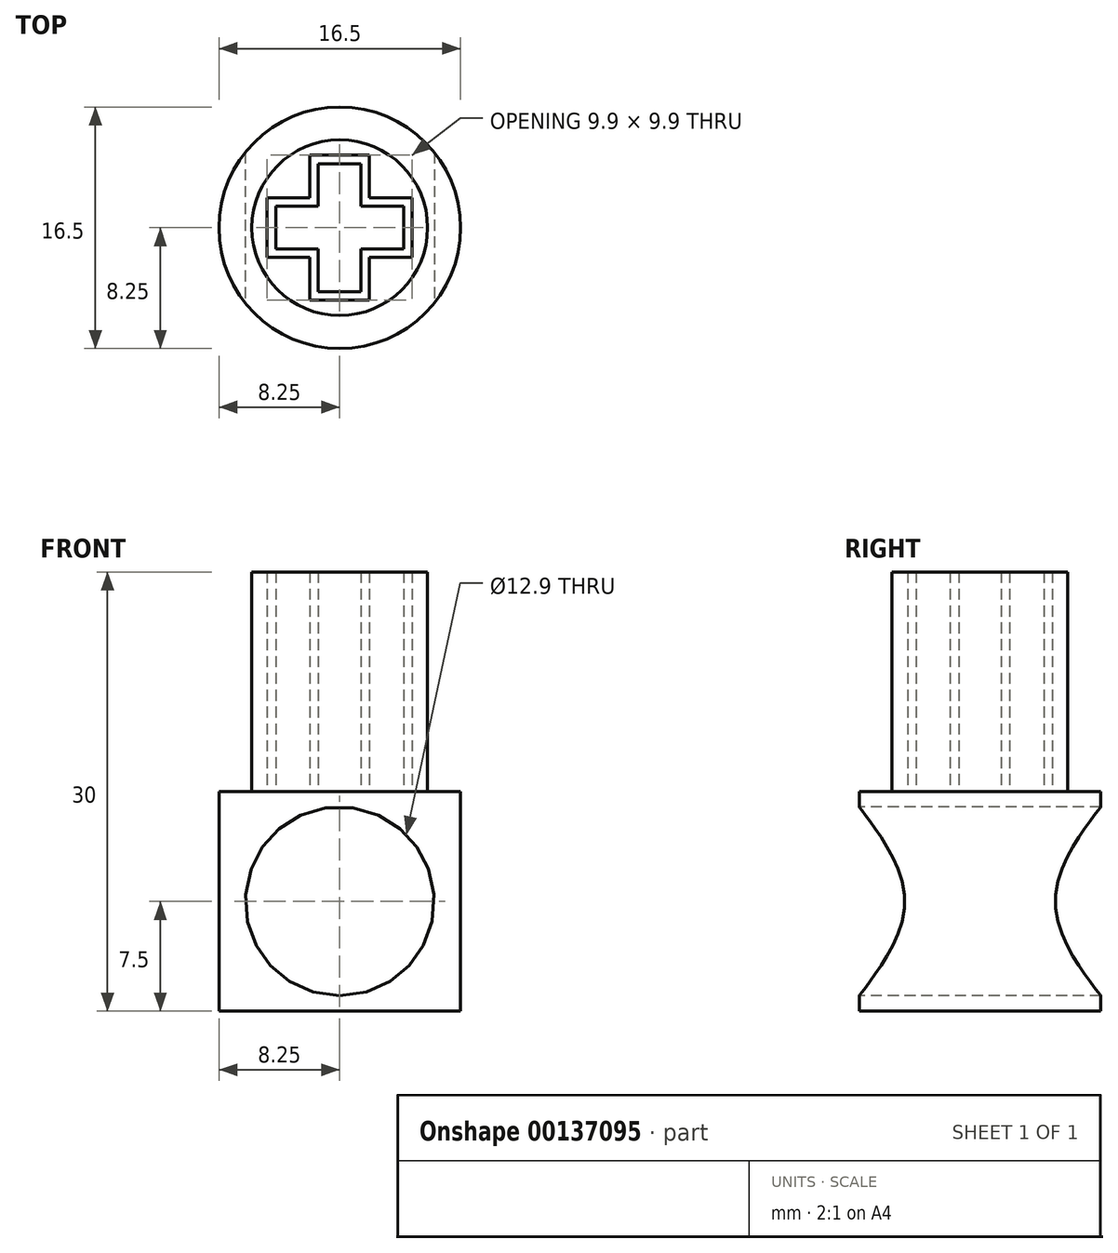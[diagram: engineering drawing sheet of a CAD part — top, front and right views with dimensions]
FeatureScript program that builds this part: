
annotation { "Feature Type Name" : "Feature", "Feature Type Description" : "" }
export const myFeature = defineFeature(function(context is Context, id is Id, definition is map)
    precondition{}
    {
        {
            var Q0;
            Q0=qCreatedBy(makeId("Top.planeOp"),FACE);
            var sketch = newSketch(context, id + "F0", { "sketchPlane" : qUnion([Q0])});
            skCircle(sketch, "E0", {"center": v(0, 0) * mm, "radius": 8.25 * mm});
            skSolve(sketch);
        }
        {
            var Q0;
            Q0 = qSketchRegion(id + "F0", true);
            extrude(context, id + "F1", {"entities" : qUnion([Q0]), "depth" : 15 * mm});
        }
        {
            var Q0;
            Q0=makeQuery(id+"F1.opExtrude","CAP_FACE",FACE,{"disambiguationData":[OSD([sQuery(id+"F0.wireOp",EDGE,"E0")])],"isStart":false});
            var sketch = newSketch(context, id + "F2", { "sketchPlane" : qUnion([Q0])});
            skLineSegment(sketch, "E1.bottom", {"start": v(-1.46, 4.38) * mm, "end": v(1.46, 4.38) * mm});
            skLineSegment(sketch, "E1.top", {"start": v(-1.46, -4.38) * mm, "end": v(1.46, -4.38) * mm});
            skLineSegment(sketch, "E1.left", {"start": v(-1.46, 4.38) * mm, "end": v(-1.46, 1.46) * mm});
            skLineSegment(sketch, "E1.right", {"start": v(1.46, 4.38) * mm, "end": v(1.46, 1.46) * mm});
            skPoint(sketch, "E1.middle", {"position": v(0, 0) * mm});
            skLineSegment(sketch, "E2.bottom", {"start": v(-4.38, 1.46) * mm, "end": v(-1.46, 1.46) * mm});
            skLineSegment(sketch, "E2.top", {"start": v(-4.38, -1.46) * mm, "end": v(-1.46, -1.46) * mm});
            skLineSegment(sketch, "E2.left", {"start": v(-4.38, 1.46) * mm, "end": v(-4.38, -1.46) * mm});
            skLineSegment(sketch, "E2.right", {"start": v(4.38, 1.46) * mm, "end": v(4.38, -1.46) * mm});
            skLineSegment(sketch, "E3.trimOffspring", {"start": v(-1.46, -1.46) * mm, "end": v(-1.46, -4.38) * mm});
            skLineSegment(sketch, "E4.trimOffspring", {"start": v(1.46, 1.46) * mm, "end": v(4.38, 1.46) * mm});
            skLineSegment(sketch, "E5.trimOffspring", {"start": v(1.46, -1.46) * mm, "end": v(1.46, -4.38) * mm});
            skLineSegment(sketch, "E6.trimOffspring", {"start": v(1.46, -1.46) * mm, "end": v(4.38, -1.46) * mm});
            skSolve(sketch);
        }
        {
            var Q0;
            Q0 = qSketchRegion(id + "F2", true);
            extrude(context, id + "F3", {"entities" : qUnion([Q0]), "operationType" : NewBodyOperationType.ADD, "depth" : 15 * mm});
        }
        {
            var Q0;
            Q0=makeQuery(id+"F1.opExtrude","CAP_FACE",FACE,{"disambiguationData":[OSD([sQuery(id+"F0.wireOp",EDGE,"E0")])],"isStart":false});
            var sketch = newSketch(context, id + "F4", { "sketchPlane" : qUnion([Q0])});
            skLineSegment(sketch, "E7.0", {"start": v(-2.03, 4.95) * mm, "end": v(2.03, 4.95) * mm});
            skLineSegment(sketch, "E7.1", {"start": v(-2.03, -2.03) * mm, "end": v(-2.03, -4.95) * mm});
            skLineSegment(sketch, "E7.2", {"start": v(-4.95, -2.03) * mm, "end": v(-2.03, -2.03) * mm});
            skLineSegment(sketch, "E7.3", {"start": v(-4.95, 2.03) * mm, "end": v(-4.95, -2.03) * mm});
            skLineSegment(sketch, "E7.4", {"start": v(-4.95, 2.03) * mm, "end": v(-2.03, 2.03) * mm});
            skLineSegment(sketch, "E7.5", {"start": v(-2.03, -4.95) * mm, "end": v(2.03, -4.95) * mm});
            skLineSegment(sketch, "E7.6", {"start": v(-2.03, 4.95) * mm, "end": v(-2.03, 2.03) * mm});
            skLineSegment(sketch, "E7.7", {"start": v(2.03, -2.03) * mm, "end": v(2.03, -4.95) * mm});
            skLineSegment(sketch, "E7.8", {"start": v(2.03, -2.03) * mm, "end": v(4.95, -2.03) * mm});
            skLineSegment(sketch, "E7.9", {"start": v(4.95, 2.03) * mm, "end": v(4.95, -2.03) * mm});
            skLineSegment(sketch, "E7.10", {"start": v(2.03, 2.03) * mm, "end": v(4.95, 2.03) * mm});
            skLineSegment(sketch, "E7.11", {"start": v(2.03, 4.95) * mm, "end": v(2.03, 2.03) * mm});
            skCircle(sketch, "E8.0", {"center": v(0, 0) * mm, "radius": 6 * mm});
            skSolve(sketch);
        }
        {
            var Q0;
            Q0 = qSketchRegion(id + "F4", true);
            var Q1;
            Q1=makeQuery(id+"F3.opExtrude","CAP_FACE",FACE,{"disambiguationData":[OSD([sQuery(id+"F2.wireOp",EDGE,"E1.bottom"),sQuery(id+"F2.wireOp",EDGE,"E1.top"),sQuery(id+"F2.wireOp",EDGE,"E1.left"),sQuery(id+"F2.wireOp",EDGE,"E1.right"),sQuery(id+"F2.wireOp",EDGE,"E2.bottom"),sQuery(id+"F2.wireOp",EDGE,"E2.top"),sQuery(id+"F2.wireOp",EDGE,"E2.left"),sQuery(id+"F2.wireOp",EDGE,"E2.right"),sQuery(id+"F2.wireOp",EDGE,"E3.trimOffspring"),sQuery(id+"F2.wireOp",EDGE,"E4.trimOffspring"),sQuery(id+"F2.wireOp",EDGE,"E5.trimOffspring"),sQuery(id+"F2.wireOp",EDGE,"E6.trimOffspring")])],"isStart":false});
            extrude(context, id + "F5", {"entities" : qUnion([Q0]), "endBound" : BoundingType.UP_TO_SURFACE, "endBoundEntityFace" : qUnion([Q1]), "depth" : 25 * mm});
        }
        {
            var Q0;
            Q0=qCreatedBy(makeId("Front.planeOp"),FACE);
            var sketch = newSketch(context, id + "F6", { "sketchPlane" : qUnion([Q0])});
            skCircle(sketch, "E9", {"center": v(0, 7.5) * mm, "radius": 6.45 * mm});
            skLineSegment(sketch, "E10", {"start": v(0, 0) * mm, "end": v(0, 15) * mm, "construction": true});
            skSolve(sketch);
        }
        {
            var Q0;
            Q0 = qSketchRegion(id + "F6", true);
            extrude(context, id + "F7", {"entities" : qUnion([Q0]), "operationType" : NewBodyOperationType.REMOVE, "endBound" : BoundingType.SYMMETRIC, "oppositeDirection" : true, "depth" : 25 * mm});
        }
    });
